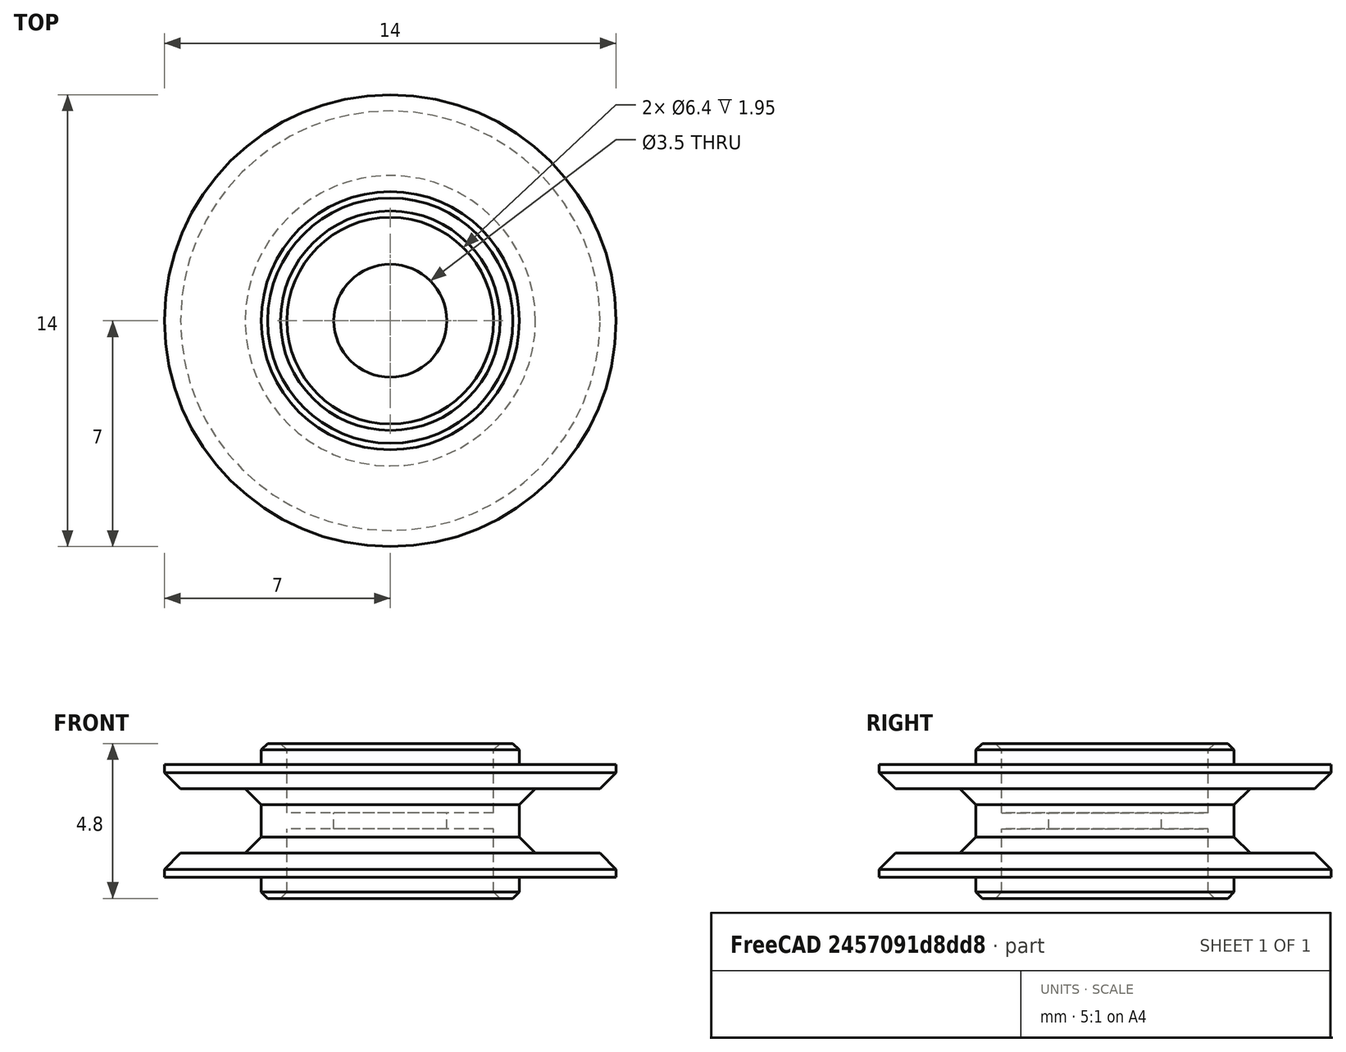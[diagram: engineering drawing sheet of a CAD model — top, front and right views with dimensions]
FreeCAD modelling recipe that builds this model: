
FCSTD DOCUMENT  (FreeCAD 0.15R4671 (Git))
Label: small_pulley_w_bearing
License: All rights reserved
LicenseURL: http://en.wikipedia.org/wiki/All_rights_reserved
objects: Part::Cylinder×8, Part::MultiFuse×2, Part::Chamfer×2, Part::Cut×1
note: 13 computed .brp shape members not serialized (recipe doc carries the construction recipe); baked Part::Feature solids carry a one-line shape summary decoded from their .brp

FEATURE [Part::Cylinder] Cylinder
  Angle = 360
  Height = 4
  Radius = 4
FEATURE [Part::Cylinder] Cylinder001
  Angle = 360
  Height = 0.75
  Placement = pos=(0,0,0.25) rot=(0,0,1;0rad)
  Radius = 7
FEATURE [Part::Cylinder] Cylinder003
  Angle = 360
  Height = 2.25
  Placement = pos=(0,0,2.25) rot=(0,0,1;0rad)
  Radius = 3.2
FEATURE [Part::Cylinder] Cylinder004
  Angle = 360
  Height = 10
  Placement = pos=(0,0,-1) rot=(0,0,1;0rad)
  Radius = 1.75
FEATURE [Part::Cylinder] Cylinder005
  Angle = 360
  Height = 0.4
  Placement = pos=(0,0,-0.4) rot=(0,0,1;0rad)
  Radius = 4
FEATURE [Part::Cylinder] Cylinder006
  Angle = 360
  Height = 0.75
  Placement = pos=(0,0,3) rot=(0,0,1;0rad)
  Radius = 7
FEATURE [Part::Cylinder] Cylinder007
  Angle = 360
  Height = 0.4
  Placement = pos=(0,0,4) rot=(0,0,1;0rad)
  Radius = 4
FEATURE [Part::MultiFuse] Fusion
  Shapes = -> [Cylinder,Cylinder001,Cylinder007,Cylinder006,Cylinder005]
FEATURE [Part::Cylinder] Cylinder008
  Angle = 360
  Height = 2.25
  Placement = pos=(0,0,-0.5) rot=(0,0,1;0rad)
  Radius = 3.2
FEATURE [Part::MultiFuse] Fusion001
  Shapes = -> [Cylinder008,Cylinder004,Cylinder003]
FEATURE [Part::Cut] Cut
  Base = -> Fusion
  Tool = -> Fusion001
FEATURE [Part::Chamfer] Chamfer
  Base = -> Cut
  Edges = 4 edges r=0.5: [Edge13,Edge16,Edge20,Edge22]
FEATURE [Part::Chamfer] Chamfer001
  Base = -> Chamfer
  Edges = 4 edges r=0.2: [Edge13,Edge16,Edge31,Edge35]
